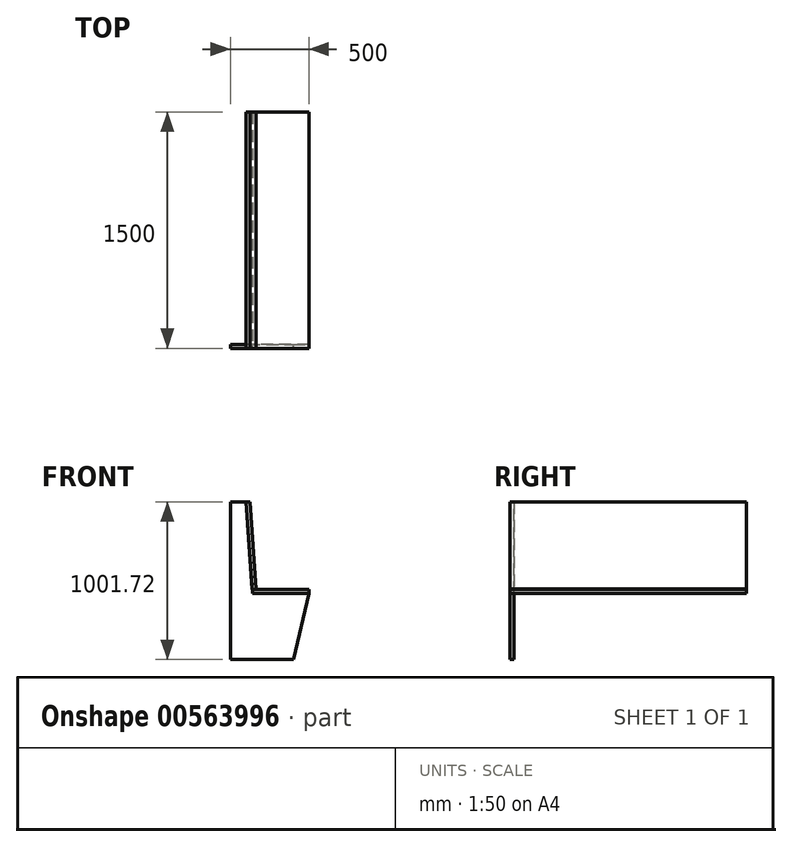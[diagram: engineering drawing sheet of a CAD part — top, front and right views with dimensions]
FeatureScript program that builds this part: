
annotation { "Feature Type Name" : "Feature", "Feature Type Description" : "" }
export const myFeature = defineFeature(function(context is Context, id is Id, definition is map)
    precondition{}
    {
        {
            var Q0;
            Q0=qCreatedBy(makeId("Front.planeOp"),FACE);
            var sketch = newSketch(context, id + "F0", { "sketchPlane" : qUnion([Q0])});
            skLineSegment(sketch, "E0", {"start": v(0, 0) * mm, "end": v(2000, 0) * mm, "construction": true});
            skLineSegment(sketch, "E1", {"start": v(0, 0) * mm, "end": v(0, 2000) * mm, "construction": true});
            skLineSegment(sketch, "E2", {"start": v(0, 0) * mm, "end": v(400, 0) * mm});
            skLineSegment(sketch, "E3", {"start": v(400, 0) * mm, "end": v(500, 420) * mm});
            skLineSegment(sketch, "E4", {"start": v(500, 420) * mm, "end": v(140, 420) * mm});
            skLineSegment(sketch, "E5", {"start": v(140, 420) * mm, "end": v(100, 1000) * mm});
            skLineSegment(sketch, "E6", {"start": v(100, 1000) * mm, "end": v(0, 1000) * mm});
            skLineSegment(sketch, "E7", {"start": v(0, 1000) * mm, "end": v(0, 0) * mm});
            skSolve(sketch);
        }
        {
            var Q0;
            Q0=makeQuery(id+"F0.imprint","IMPRINT",FACE,{"disambiguationData":[TD([[makeQuery(id+"F0.imprint","IMPRINT",EDGE,{"derivedFrom":sQuery(id+"F0.wireOp",EDGE,"E2")}),1.0]])]});
            var Q1;
            Q1=makeQuery(id+"F0.imprint","IMPRINT",FACE,{"disambiguationData":[TD([[makeQuery(id+"F0.imprint","IMPRINT",EDGE,{"derivedFrom":sQuery(id+"F0.wireOp",EDGE,"E3")}),-1.0]])]});
            extrude(context, id + "F1", {"entities" : qUnion([Q0, Q1]), "depth" : 25 * mm, "offsetDistance" : 25 * mm});
        }
        {
            var Q0;
            Q0=makeQuery(id+"F1.opExtrude","CAP_FACE",FACE,{"disambiguationData":[OSD([sQuery(id+"F0.wireOp",EDGE,"E2"),sQuery(id+"F0.wireOp",EDGE,"E3"),sQuery(id+"F0.wireOp",EDGE,"E4"),sQuery(id+"F0.wireOp",EDGE,"E5"),sQuery(id+"F0.wireOp",EDGE,"E6"),sQuery(id+"F0.wireOp",EDGE,"E7")])],"isStart":false});
            var sketch = newSketch(context, id + "F2", { "sketchPlane" : qUnion([Q0])});
            skLineSegment(sketch, "E8.bottom", {"start": v(140, 420) * mm, "end": v(500, 420) * mm});
            skLineSegment(sketch, "E8.top", {"start": v(140, 445) * mm, "end": v(500, 445) * mm});
            skLineSegment(sketch, "E8.left", {"start": v(140, 420) * mm, "end": v(140, 445) * mm});
            skLineSegment(sketch, "E8.right", {"start": v(500, 420) * mm, "end": v(500, 445) * mm});
            skSolve(sketch);
        }
        {
            var Q0;
            Q0 = qSketchRegion(id + "F2", true);
            extrude(context, id + "F3", {"entities" : qUnion([Q0]), "oppositeDirection" : true, "depth" : 1500 * mm, "offsetDistance" : 25 * mm});
        }
        {
            var Q0;
            Q0=makeQuery(id+"F1.opExtrude","CAP_FACE",FACE,{"disambiguationData":[OSD([sQuery(id+"F0.wireOp",EDGE,"E2"),sQuery(id+"F0.wireOp",EDGE,"E3"),sQuery(id+"F0.wireOp",EDGE,"E4"),sQuery(id+"F0.wireOp",EDGE,"E5"),sQuery(id+"F0.wireOp",EDGE,"E6"),sQuery(id+"F0.wireOp",EDGE,"E7")])],"isStart":false});
            var sketch = newSketch(context, id + "F4", { "sketchPlane" : qUnion([Q0])});
            skLineSegment(sketch, "E9.bottom", {"start": v(100, 1000) * mm, "end": v(124.94, 1001.72) * mm});
            skLineSegment(sketch, "E9.top", {"start": v(138.28, 444.88) * mm, "end": v(163.22, 446.6) * mm});
            skLineSegment(sketch, "E9.left", {"start": v(100, 1000) * mm, "end": v(138.28, 444.88) * mm});
            skLineSegment(sketch, "E9.right", {"start": v(124.94, 1001.72) * mm, "end": v(163.22, 446.6) * mm});
            skSolve(sketch);
        }
        {
            var Q0;
            Q0 = qSketchRegion(id + "F4", true);
            extrude(context, id + "F5", {"entities" : qUnion([Q0]), "oppositeDirection" : true, "depth" : 1500 * mm, "offsetDistance" : 25 * mm});
        }
    });
